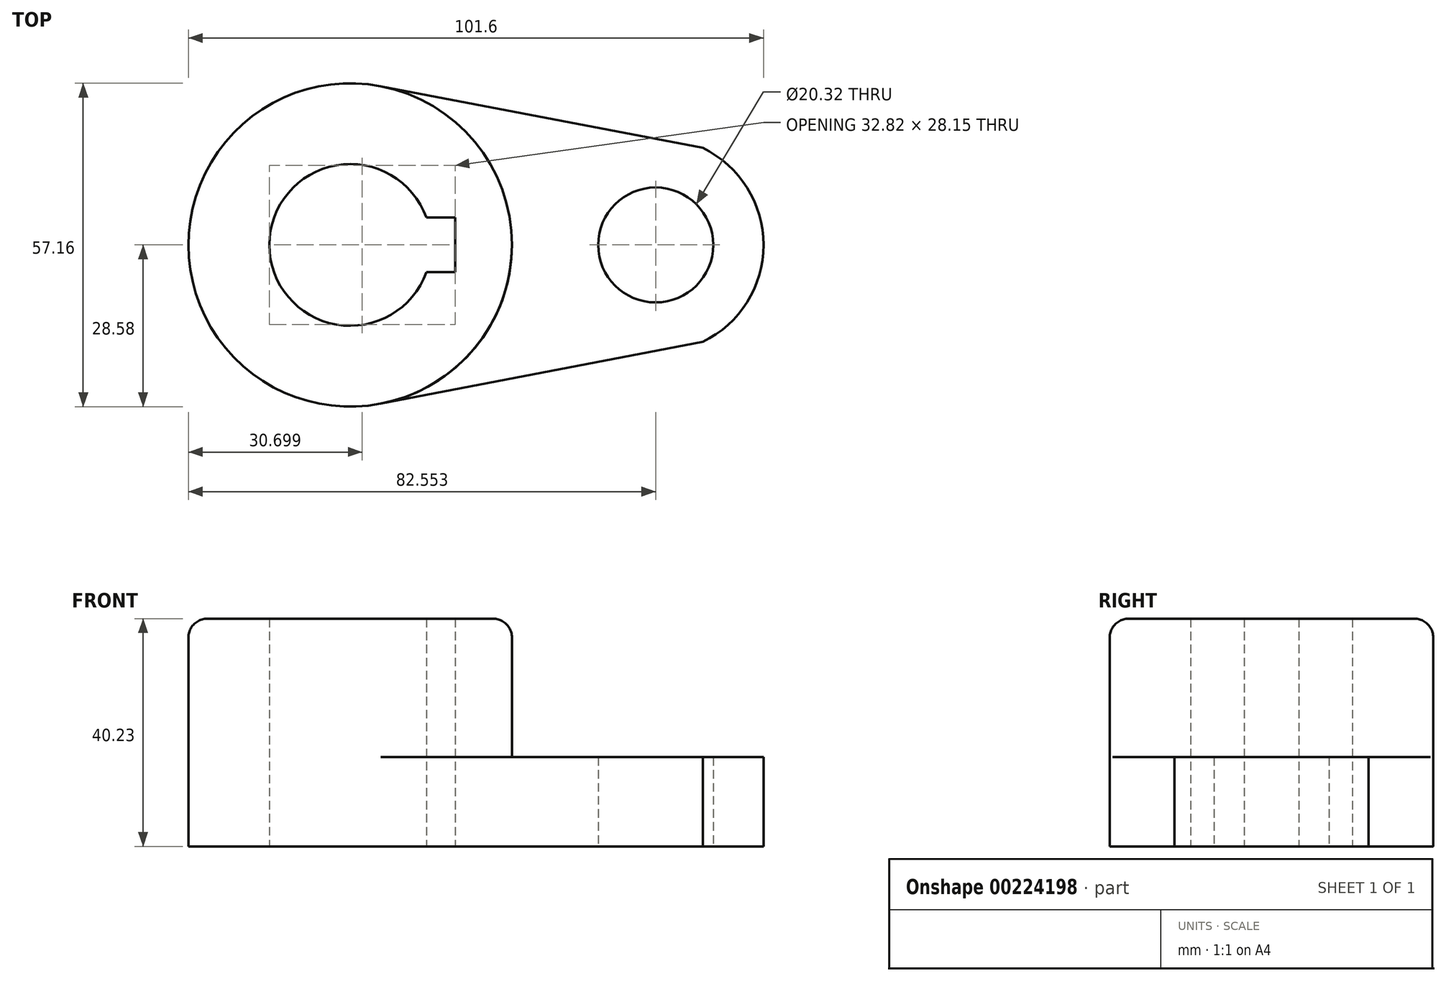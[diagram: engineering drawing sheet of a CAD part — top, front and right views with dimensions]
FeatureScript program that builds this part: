
annotation { "Feature Type Name" : "Feature", "Feature Type Description" : "" }
export const myFeature = defineFeature(function(context is Context, id is Id, definition is map)
    precondition{}
    {
        {
            var Q0;
            Q0=qCreatedBy(makeId("Top.planeOp"),FACE);
            var sketch = newSketch(context, id + "F0", { "sketchPlane" : qUnion([Q0])});
            skCircle(sketch, "E0", {"center": v(-52.17, 0) * mm, "radius": 28.58 * mm});
            skArc(sketch, "E1", {"start": v(-38.72, 4.83) * mm, "mid": v(-66.46, 0) * mm, "end": v(-38.72, -4.83) * mm});
            skArc(sketch, "E2", {"start": v(10.1, -17.15) * mm, "mid": v(20.85, 0) * mm, "end": v(10.1, 17.15) * mm});
            skCircle(sketch, "E3", {"center": v(1.8, 0) * mm, "radius": 10.16 * mm});
            skLineSegment(sketch, "E4", {"start": v(10.1, 17.15) * mm, "end": v(-46.79, 28.06) * mm});
            skLineSegment(sketch, "E5", {"start": v(10.1, -17.15) * mm, "end": v(-46.79, -28.06) * mm});
            skLineSegment(sketch, "E6.bottom", {"start": v(-33.64, 4.83) * mm, "end": v(-38.72, 4.83) * mm});
            skLineSegment(sketch, "E6.top", {"start": v(-33.64, -4.83) * mm, "end": v(-38.72, -4.83) * mm});
            skLineSegment(sketch, "E6.left", {"start": v(-33.64, 4.83) * mm, "end": v(-33.64, -4.83) * mm});
            skSolve(sketch);
        }
        {
            var Q0;
            Q0=makeQuery(id+"F0.imprint","IMPRINT",FACE,{"disambiguationData":[TD([[makeQuery(id+"F0.imprint","IMPRINT",EDGE,{"derivedFrom":sQuery(id+"F0.wireOp",EDGE,"E1")}),-1.0]])]});
            extrude(context, id + "F1", {"entities" : qUnion([Q0]), "depth" : 40.23 * mm});
        }
        {
            var Q0;
            Q0 = qSketchRegion(id + "F0", true);
            extrude(context, id + "F2", {"entities" : qUnion([Q0]), "operationType" : NewBodyOperationType.ADD, "depth" : 15.77 * mm});
        }
        {
            var Q0;
            Q0=makeQuery(id+"F1.opExtrude","CAP_EDGE",EDGE,{"disambiguationData":[OSD([sQuery(id+"F0.wireOp",EDGE,"E0")])],"isStart":false});
            fillet(context, id + "F3", {"entities" : qUnion([Q0]), "radius" : 3.3 * mm, "tangentPropagation" : true, "allowEdgeOverflow" : false});
        }
    });
